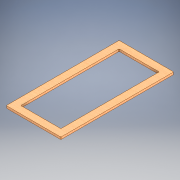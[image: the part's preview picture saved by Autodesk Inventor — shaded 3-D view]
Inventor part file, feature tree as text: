
AUTODESK INVENTOR PART (.ipt)
format: ipt  version: 2020 (Build 240168000, 168)  size: 138,752 bytes
history: native  units: mm
features: extrude x1, sketch x1
ambient origin geometry x8: Origin, YZ Plane, XZ Plane, XY Plane, X Axis, Y Axis, Z Axis, Center Point
bodies: Solide1 (feature_tree)
feature tree (2):
  extrude  "Extrusion1"  Depth=150.0mm
  sketch  "Esquisse1"
